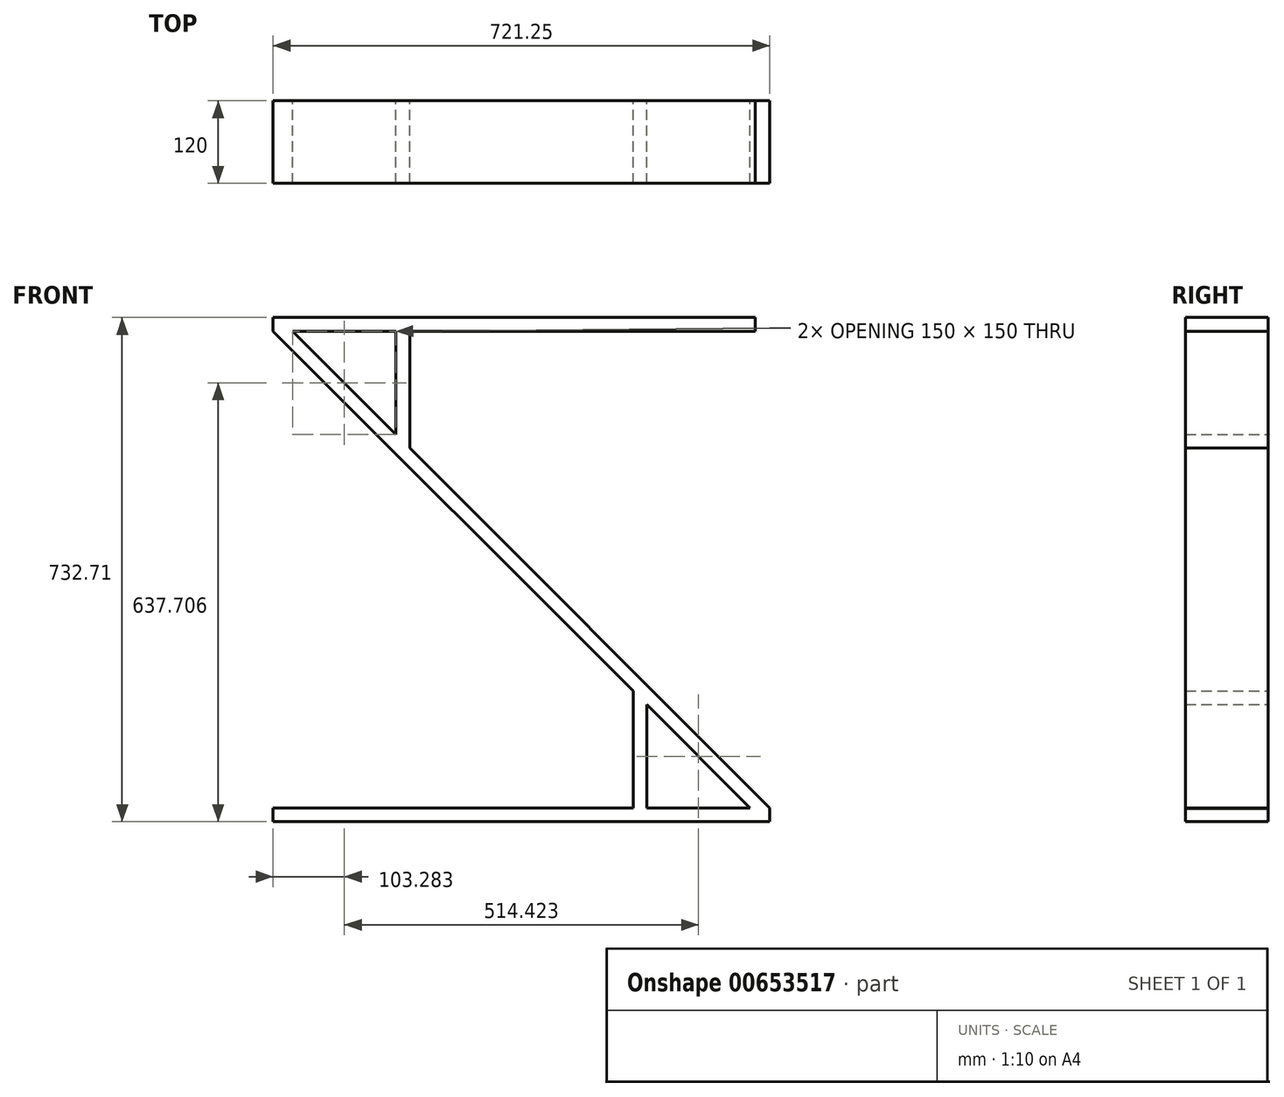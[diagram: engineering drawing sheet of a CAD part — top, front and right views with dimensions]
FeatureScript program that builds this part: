
annotation { "Feature Type Name" : "Feature", "Feature Type Description" : "" }
export const myFeature = defineFeature(function(context is Context, id is Id, definition is map)
    precondition{}
    {
        {
            var Q0;
            Q0=qCreatedBy(makeId("Front.planeOp"),FACE);
            var sketch = newSketch(context, id + "F0", { "sketchPlane" : qUnion([Q0])});
            skLineSegment(sketch, "E0.bottom", {"start": v(356.16, 518.88) * mm, "end": v(-343.84, 518.88) * mm});
            skLineSegment(sketch, "E0.top", {"start": v(356.16, 498.88) * mm, "end": v(-343.84, 498.88) * mm});
            skLineSegment(sketch, "E0.left", {"start": v(356.16, 518.88) * mm, "end": v(356.16, 498.88) * mm});
            skLineSegment(sketch, "E0.right", {"start": v(-343.84, 518.88) * mm, "end": v(-343.84, 498.88) * mm});
            skLineSegment(sketch, "E1.bottom", {"start": v(377.4, -194.09) * mm, "end": v(-315.56, 498.88) * mm});
            skLineSegment(sketch, "E1.top", {"start": v(348.87, -193.83) * mm, "end": v(-343.84, 498.88) * mm});
            skLineSegment(sketch, "E1.left", {"start": v(377.4, -194.09) * mm, "end": v(376.95, -194.55) * mm});
            skLineSegment(sketch, "E2.0", {"start": v(-315.56, 498.88) * mm, "end": v(377.4, -194.09) * mm, "construction": true});
            skLineSegment(sketch, "E2.1", {"start": v(377.4, -194.09) * mm, "end": v(377.4, -194.09) * mm});
            skLineSegment(sketch, "E3.bottom", {"start": v(376.95, -193.83) * mm, "end": v(-343.84, -193.83) * mm});
            skLineSegment(sketch, "E3.top", {"start": v(376.95, -213.83) * mm, "end": v(-343.84, -213.83) * mm});
            skLineSegment(sketch, "E3.left", {"start": v(376.95, -193.83) * mm, "end": v(376.95, -213.83) * mm});
            skLineSegment(sketch, "E3.right", {"start": v(-343.84, -193.83) * mm, "end": v(-343.84, -213.83) * mm});
            skLineSegment(sketch, "E4.left", {"start": v(-165.56, 498.88) * mm, "end": v(-165.56, 348.88) * mm});
            skLineSegment(sketch, "E4.right", {"start": v(-145.56, 498.88) * mm, "end": v(-145.56, 328.88) * mm});
            skLineSegment(sketch, "E5.left", {"start": v(178.87, -23.83) * mm, "end": v(178.87, -193.83) * mm});
            skLineSegment(sketch, "E5.right", {"start": v(198.87, -43.83) * mm, "end": v(198.87, -193.83) * mm});
            skSolve(sketch);
        }
        {
            var Q0;
            Q0 = qSketchRegion(id + "F0", true);
            extrude(context, id + "F1", {"entities" : qUnion([Q0]), "depth" : 120 * mm, "offsetDistance" : 25 * mm});
        }
    });
